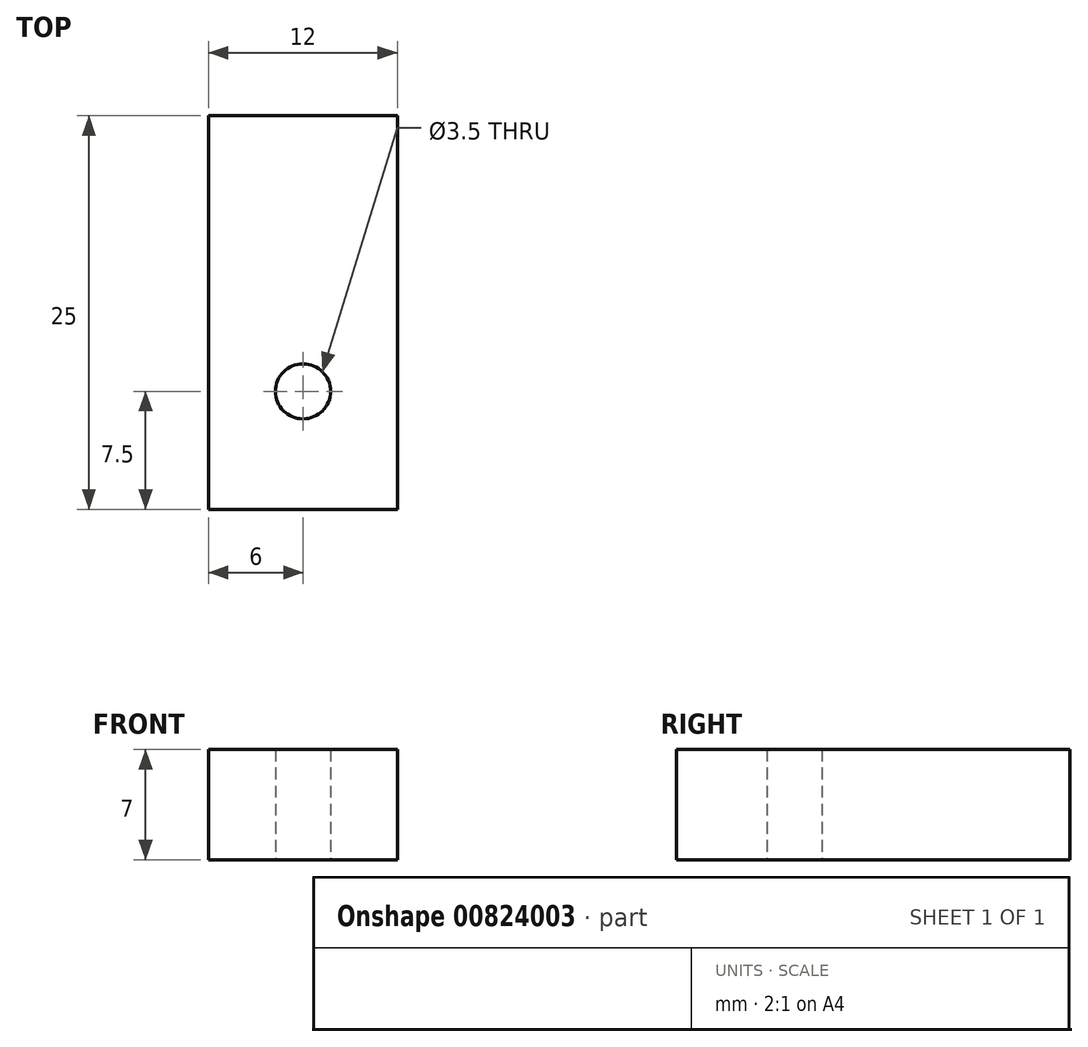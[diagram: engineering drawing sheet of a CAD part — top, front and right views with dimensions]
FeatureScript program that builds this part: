
annotation { "Feature Type Name" : "Feature", "Feature Type Description" : "" }
export const myFeature = defineFeature(function(context is Context, id is Id, definition is map)
    precondition{}
    {
        {
            var Q0;
            Q0=qCreatedBy(makeId("Top.planeOp"),FACE);
            var sketch = newSketch(context, id + "F0", { "sketchPlane" : qUnion([Q0])});
            skLineSegment(sketch, "E0.bottom", {"start": v(0, 0) * mm, "end": v(12, 0) * mm});
            skLineSegment(sketch, "E0.top", {"start": v(0, 25) * mm, "end": v(12, 25) * mm});
            skLineSegment(sketch, "E0.left", {"start": v(0, 0) * mm, "end": v(0, 25) * mm});
            skLineSegment(sketch, "E0.right", {"start": v(12, 0) * mm, "end": v(12, 25) * mm});
            skCircle(sketch, "E1", {"center": v(6, 7.5) * mm, "radius": 1.75 * mm});
            skSolve(sketch);
        }
        {
            var Q0;
            Q0 = qSketchRegion(id + "F0", true);
            extrude(context, id + "F1", {"entities" : qUnion([Q0]), "depth" : 7 * mm, "offsetDistance" : 25 * mm});
        }
    });
